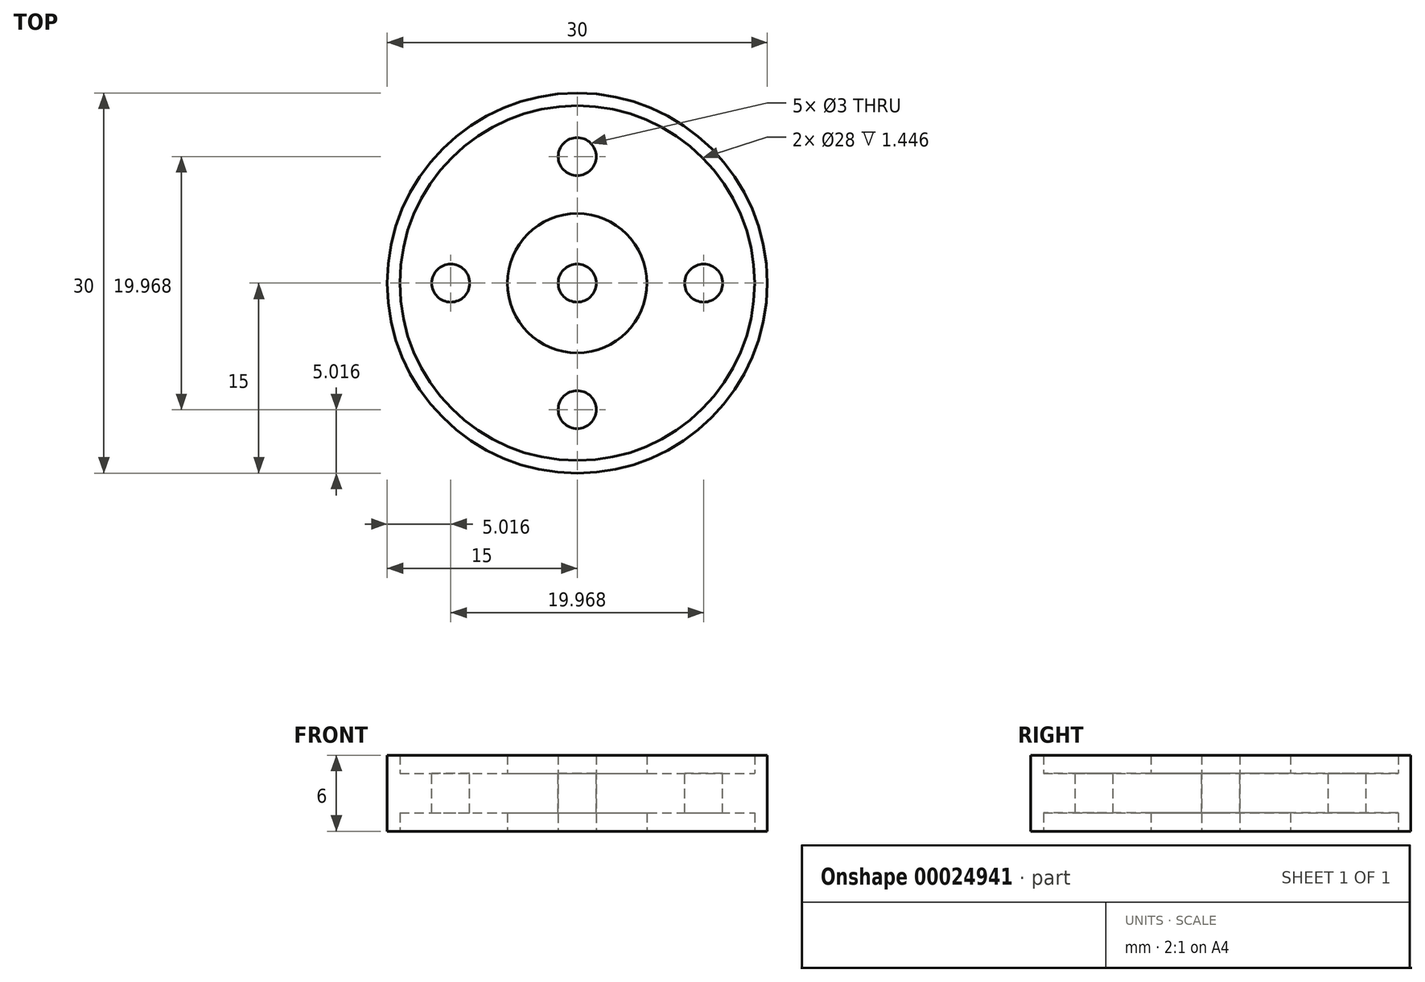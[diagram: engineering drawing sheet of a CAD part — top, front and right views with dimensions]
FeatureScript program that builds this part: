
annotation { "Feature Type Name" : "Feature", "Feature Type Description" : "" }
export const myFeature = defineFeature(function(context is Context, id is Id, definition is map)
    precondition{}
    {
        {
            var Q0;
            Q0=qCreatedBy(makeId("Front.planeOp"),FACE);
            var sketch = newSketch(context, id + "F0", { "sketchPlane" : qUnion([Q0])});
            skLineSegment(sketch, "E0", {"start": v(0, -8.37) * mm, "end": v(0, 9.87) * mm, "construction": true});
            skLineSegment(sketch, "E1.bottom", {"start": v(1.5, 3.42) * mm, "end": v(5.5, 3.42) * mm});
            skLineSegment(sketch, "E1.top", {"start": v(1.5, -2.58) * mm, "end": v(5.5, -2.58) * mm});
            skLineSegment(sketch, "E1.left", {"start": v(1.5, 3.42) * mm, "end": v(1.5, -2.58) * mm});
            skLineSegment(sketch, "E1.right", {"start": v(5.5, 3.42) * mm, "end": v(5.5, 1.97) * mm});
            skLineSegment(sketch, "E2.bottom", {"start": v(5.5, 1.97) * mm, "end": v(14, 1.97) * mm});
            skLineSegment(sketch, "E2.top", {"start": v(5.5, -1.14) * mm, "end": v(14, -1.14) * mm});
            skLineSegment(sketch, "E3.bottom", {"start": v(14, 3.42) * mm, "end": v(15, 3.42) * mm});
            skLineSegment(sketch, "E3.top", {"start": v(14, -2.58) * mm, "end": v(15, -2.58) * mm});
            skLineSegment(sketch, "E3.left", {"start": v(14, 3.42) * mm, "end": v(14, 1.97) * mm});
            skLineSegment(sketch, "E3.right", {"start": v(15, 3.42) * mm, "end": v(15, -2.58) * mm});
            skLineSegment(sketch, "E4.trimOffspring", {"start": v(14, -1.14) * mm, "end": v(14, -2.58) * mm});
            skLineSegment(sketch, "E5.trimOffspring", {"start": v(5.5, -1.14) * mm, "end": v(5.5, -2.58) * mm});
            skLineSegment(sketch, "E6.bottom", {"start": v(15, 1.37) * mm, "end": v(18.27, 1.37) * mm});
            skLineSegment(sketch, "E6.top", {"start": v(15, 4.72) * mm, "end": v(18.27, 4.72) * mm});
            skLineSegment(sketch, "E6.left", {"start": v(15, 1.37) * mm, "end": v(15, 4.72) * mm});
            skLineSegment(sketch, "E6.right", {"start": v(18.27, 1.37) * mm, "end": v(18.27, 4.72) * mm});
            skLineSegment(sketch, "E7", {"start": v(19.7, 0.58) * mm, "end": v(19.7, 5.92) * mm, "construction": true});
            skSolve(sketch);
        }
        {
            var Q0;
            Q0=makeQuery(id+"F0.imprint","IMPRINT",FACE,{"disambiguationData":[TD([[makeQuery(id+"F0.imprint","IMPRINT",EDGE,{"derivedFrom":sQuery(id+"F0.wireOp",EDGE,"E1.bottom")}),-1.0]])]});
            var Q1;
            Q1=sQuery(id+"F0.wireOp",EDGE,"E0");
            revolve(context, id + "F1", {"entities" : qUnion([Q0]), "axis" : qUnion([Q1]), "revolveType" : RevolveType.FULL});
        }
        {
            var Q0;
            Q0=makeQuery(id+"F1.opRevolve","SWEPT_FACE",FACE,{"disambiguationData":[OSD([sQuery(id+"F0.wireOp",EDGE,"E2.bottom")])]});
            var sketch = newSketch(context, id + "F2", { "sketchPlane" : qUnion([Q0])});
            skCircle(sketch, "E8", {"center": v(0, 9.98) * mm, "radius": 1.5 * mm});
            skCircle(sketch, "E9.1.0", {"center": v(-9.98, 0) * mm, "radius": 1.5 * mm});
            skCircle(sketch, "E9.2.0", {"center": v(0, -9.98) * mm, "radius": 1.5 * mm});
            skCircle(sketch, "E9.3.0", {"center": v(9.98, 0) * mm, "radius": 1.5 * mm});
            skPoint(sketch, "E9.center", {"position": v(0, 0) * mm});
            skSolve(sketch);
        }
        {
            var Q0;
            Q0=makeQuery(id+"F2.imprint","IMPRINT",FACE,{"disambiguationData":[TD([[makeQuery(id+"F2.imprint","IMPRINT",EDGE,{"derivedFrom":sQuery(id+"F2.wireOp",EDGE,"E9.1.0")}),1.0]])]});
            var Q1;
            Q1=makeQuery(id+"F2.imprint","IMPRINT",FACE,{"disambiguationData":[TD([[makeQuery(id+"F2.imprint","IMPRINT",EDGE,{"derivedFrom":sQuery(id+"F2.wireOp",EDGE,"E8")}),1.0]])]});
            var Q2;
            Q2=makeQuery(id+"F2.imprint","IMPRINT",FACE,{"disambiguationData":[TD([[makeQuery(id+"F2.imprint","IMPRINT",EDGE,{"derivedFrom":sQuery(id+"F2.wireOp",EDGE,"E9.3.0")}),1.0]])]});
            var Q3;
            Q3=makeQuery(id+"F2.imprint","IMPRINT",FACE,{"disambiguationData":[TD([[makeQuery(id+"F2.imprint","IMPRINT",EDGE,{"derivedFrom":sQuery(id+"F2.wireOp",EDGE,"E9.2.0")}),1.0]])]});
            extrude(context, id + "F3", {"entities" : qUnion([Q0, Q1, Q2, Q3]), "operationType" : NewBodyOperationType.REMOVE, "endBound" : BoundingType.THROUGH_ALL, "oppositeDirection" : true, "depth" : 25 * mm});
        }
    });
